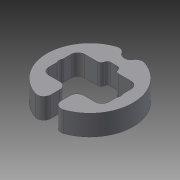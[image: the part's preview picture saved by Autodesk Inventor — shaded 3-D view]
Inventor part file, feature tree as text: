
AUTODESK INVENTOR PART (.ipt)
format: ipt  version: 2015 (Build 190159000, 159)  size: 150,528 bytes
history: native  units: mm
features: extrude x1, sketch x1
ambient origin geometry x8: Origin, YZ Plane, XZ Plane, XY Plane, X Axis, Y Axis, Z Axis, Center Point
bodies: Solid1 (feature_tree)
feature tree (2):
  extrude  "Extrusion1"  Depth=4.0mm
  sketch  "Sketch1"  dims[d2=22.0mm d3=4.0mm d5=2.0mm d6=2.0mm d7=3.0mm d8=3.0mm d10=15.0mm d11=3.0mm d13=10.5mm d14=10.5mm d15=2.0mm d16=2.0mm d17=2.0mm d18=7.0mm d19=4.0mm d20=10.5mm d21=1.0mm d22=1.0mm d23=6.0mm d24=0.0mm d25=12.0mm d26=12.5mm d27=17.5mm]
